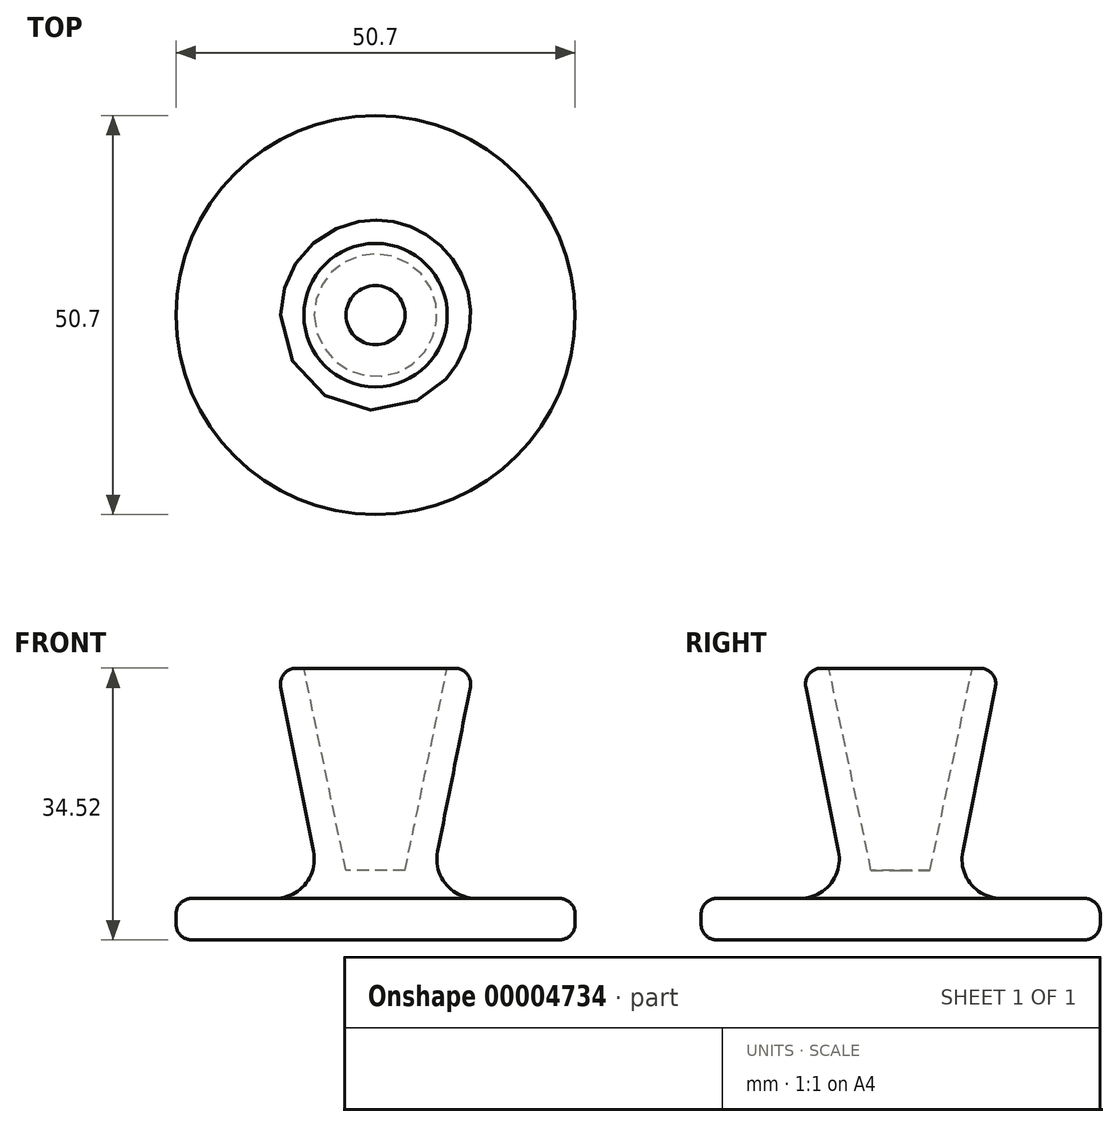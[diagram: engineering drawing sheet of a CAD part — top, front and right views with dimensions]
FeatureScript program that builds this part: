
annotation { "Feature Type Name" : "Feature", "Feature Type Description" : "" }
export const myFeature = defineFeature(function(context is Context, id is Id, definition is map)
    precondition{}
    {
        {
            var Q0;
            Q0=qCreatedBy(makeId("Front.planeOp"),FACE);
            var sketch = newSketch(context, id + "F0", { "sketchPlane" : qUnion([Q0])});
            skLineSegment(sketch, "E0", {"start": v(0, 0) * mm, "end": v(-25.35, 0) * mm});
            skLineSegment(sketch, "E1", {"start": v(-25.35, 0) * mm, "end": v(-25.35, 5.27) * mm});
            skLineSegment(sketch, "E2", {"start": v(-25.35, 5.27) * mm, "end": v(-6.7, 5.27) * mm});
            skLineSegment(sketch, "E3", {"start": v(-6.7, 5.27) * mm, "end": v(-12.52, 34.52) * mm});
            skLineSegment(sketch, "E4", {"start": v(-12.52, 34.52) * mm, "end": v(-9.1, 34.52) * mm});
            skLineSegment(sketch, "E5", {"start": v(-9.1, 34.52) * mm, "end": v(-3.75, 8.85) * mm});
            skLineSegment(sketch, "E6", {"start": v(-3.75, 8.85) * mm, "end": v(0, 8.85) * mm});
            skLineSegment(sketch, "E7", {"start": v(0, 8.85) * mm, "end": v(0, 0) * mm});
            skSolve(sketch);
        }
        {
            var Q0;
            Q0=makeQuery(id+"F0.imprint","IMPRINT",FACE,{"disambiguationData":[TD([[makeQuery(id+"F0.imprint","IMPRINT",EDGE,{"derivedFrom":sQuery(id+"F0.wireOp",EDGE,"E0")}),-1.0]])]});
            var Q1;
            Q1=sQuery(id+"F0.wireOp",EDGE,"E7");
            revolve(context, id + "F1", {"entities" : qUnion([Q0]), "axis" : qUnion([Q1]), "revolveType" : RevolveType.FULL});
        }
        {
            var Q0;
            Q0=makeQuery(id+"F1.opRevolve","SWEPT_EDGE",EDGE,{"disambiguationData":[OSD([sQuery(id+"F0.wireOp",EDGE,"E2"),sQuery(id+"F0.wireOp",EDGE,"E3")])]});
            fillet(context, id + "F2", {"entities" : qUnion([Q0]), "radius" : 5 * mm, "tangentPropagation" : true, "allowEdgeOverflow" : false});
        }
        {
            var Q0;
            Q0=makeQuery(id+"F1.opRevolve","SWEPT_FACE",FACE,{"disambiguationData":[OSD([sQuery(id+"F0.wireOp",EDGE,"E1")])]});
            var Q1;
            Q1=makeQuery(id+"F1.opRevolve","SWEPT_EDGE",EDGE,{"disambiguationData":[OSD([sQuery(id+"F0.wireOp",EDGE,"E3"),sQuery(id+"F0.wireOp",EDGE,"E4")])]});
            fillet(context, id + "F3", {"entities" : qUnion([Q0, Q1]), "radius" : 2 * mm, "tangentPropagation" : true, "allowEdgeOverflow" : false});
        }
    });
